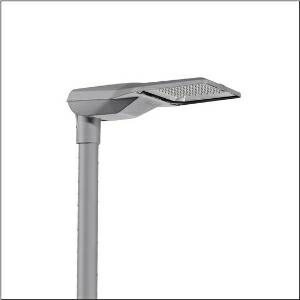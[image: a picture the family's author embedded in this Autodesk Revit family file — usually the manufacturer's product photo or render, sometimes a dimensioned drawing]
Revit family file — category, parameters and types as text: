
# Revit family: streetlight_sl_21_iq_midi___pc-r_5xe3g31g08mb_83c1
name_source: partatom
category: Lighting Fixtures
units: mm (PartAtom-declared; Revit-internal decimal feet)

## family parameters
Cut with Voids When Loaded = No
Host = Face
Light Source = No
Part Type = Normal
Room Calculation Point = No
Round Connector Dimension = Use Diameter
Shared = No

## types (1)
- --- (1 x LED, 18560 lm, 146.7 W, 3000K)
    Apparent Load = 147 VA
    CIE Flux Codes = 38 78 98 100 100
    Color Rendering = 70
    Color Temperature = 3000K
    Default Elevation = 1800 mm
    Description = Streetlight SL 21 iQ midi, mast luminaire, primary light control with lens, of PMMA, primary optical cover: cover, of toughened safety glass, transparent, light distribution: PC-R, light emission: direct distribution, primary light characteristic: asymmetric, right, installation type: post-top, side-entry, LED, High Power LED, rated luminous flux: 18.560lm, luminous efficacy: 127lm/W, light colour: 730, colour temperature: 3000K, control gear: iQ Street-Remote, control: Street-Remote, Auto-Match, Temp-Guard, Lumen-Switch, Night-Set, Smart-Wire, Light-Fading, Desk-Remote (wireless, voltage-free reading and setting of iQ features in the workshop via application-optimized NFC function/RFID function), optimised constant luminous flux control (CLO 2.0), pre-setting: linear dimming characteristic, mains connection: 230..240V, AC, 50/60Hz, start of lifetime: 147W, end of service life: 161W, reduction: 62W, luminaire housing, of diecast aluminium, powder-coated, SITECO metallic grey (DB 702S), corrosivity category C5 high according to DIN EN ISO 12944, please order mast flange separately, inclination adjustable: 0°, 5°, 10°, 15°, sealing non-destructively replaceable, multi-level sealing system, length: 644mm, width: 335mm, height: 110mm, mast flange for spigot size: 42mm (side-entry): 5XC10008XM4, 60/48mm (side-entry/post-top): 5XC10108XM2, 76/60mm (side-entry/post-top): 5XC10108XM1, mounting height: 4..8m, protection rating (complete): IP66, insulation class (complete): insulation class II (safety insulation), certification: CE, ENEC, ENEC+, VDE, impact resistance: IK10, permissible operating ambient temperature for outdoor applications: -40..+50°C, standard-compliant lighting for roads and squares, packaging unit: 1 piece

Light Distribution: PC-R
    Height = 111 mm
    Lamp = 1 x LED
    Lamp Light Flux = 18560 lm
    Lamp Power = 146.7 W
    Lamp count = 1
    Length = 644 mm
    Luminous efficacy = 127 lm/W
    Manufacturer = Siteco
    ModVariant = No
    Model = 5XE3G31G08MB
    Number of Poles = 1
    OnlyDefault = Yes
    Power Factor = 1
    Product Name = Streetlight SL 21 iQ midi | PC-R
    Product group = mast luminaire | pylon top
    ProductGroupID = 6100
    Protection Class = Protection class II
    Protection Degree = IP 66
    RLX_Detail_Level = 1
    RLX_Emergency_Light_Flux = 0 lm
    RLX_Emergency_Type = 0
    RLX_Emergency_Type_DB = No
    RlxData = <blob elided: 29397 chars, md5=74bb98f1>
    Socket = socket
    Standby Power = 0 W
    System Light Flux = 18560 lm
    System Power = 147 W
    Type Comments = factory setting: luminous flux: 100 % | dim-lin: 254 | 753 mA
    Type Image = l_1004298.jpg
    URL = http://relux.com
    VarID = @adj_071737
    Voltage = 0 V
    Weight = 0.00 kg
    Width = 336 mm

## geometry (parser evidence)
native form markers: Blend x4, Sweep x9
no freeform markers — native parametric forms only
